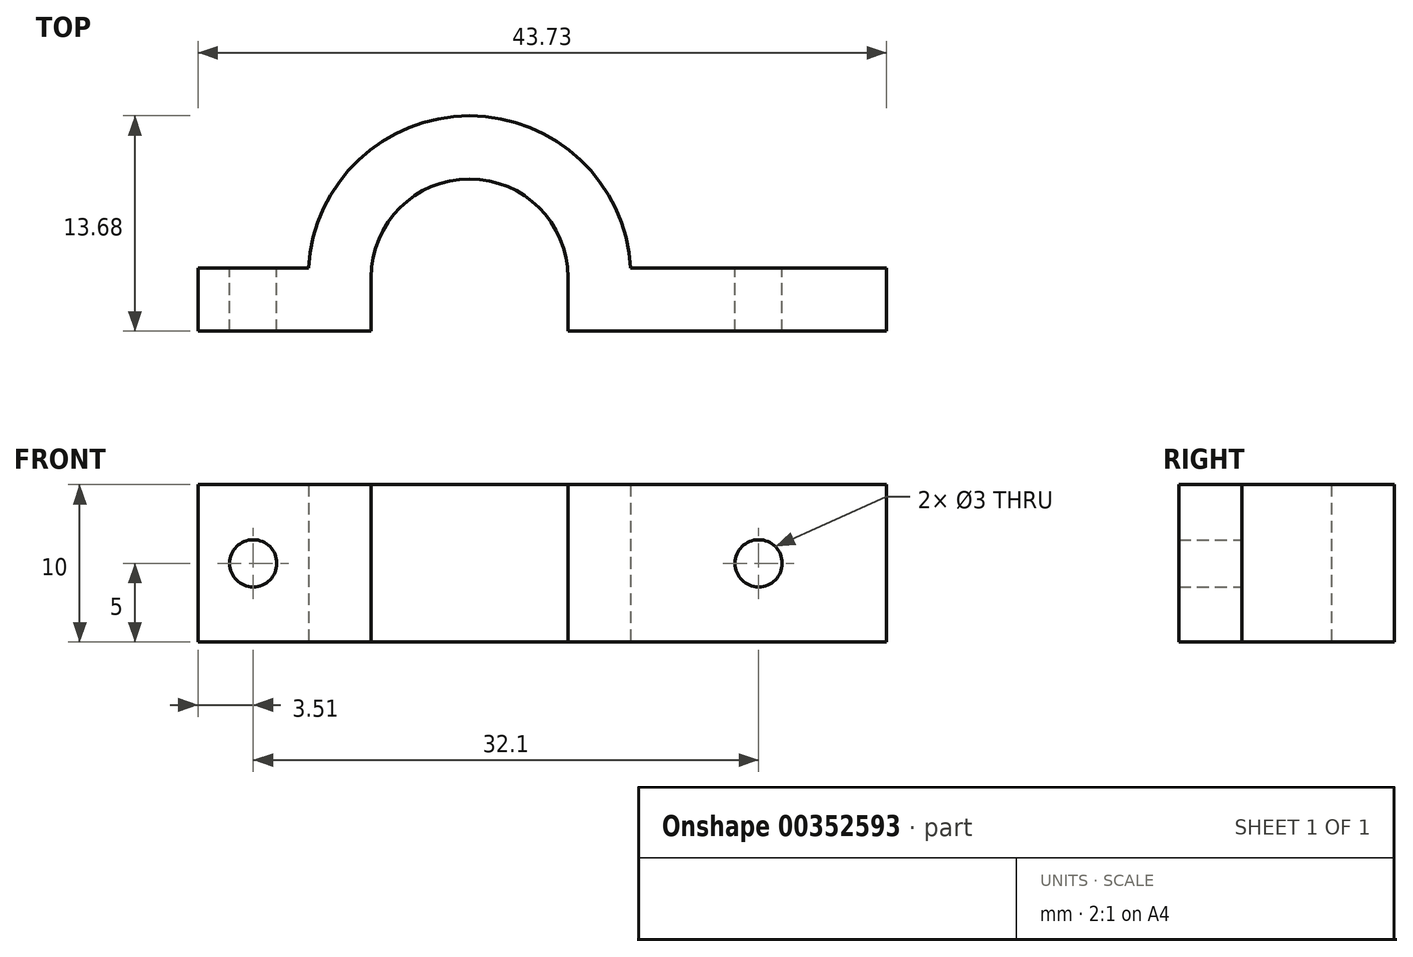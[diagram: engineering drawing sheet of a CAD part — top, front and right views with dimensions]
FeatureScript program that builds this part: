
annotation { "Feature Type Name" : "Feature", "Feature Type Description" : "" }
export const myFeature = defineFeature(function(context is Context, id is Id, definition is map)
    precondition{}
    {
        {
            var Q0;
            Q0=qCreatedBy(makeId("Top.planeOp"),FACE);
            var sketch = newSketch(context, id + "F0", { "sketchPlane" : qUnion([Q0])});
            skLineSegment(sketch, "E0", {"start": v(14.61, -13.31) * mm, "end": v(38.11, -13.31) * mm});
            skLineSegment(sketch, "E1", {"start": v(38.11, -13.31) * mm, "end": v(38.11, -9.31) * mm});
            skLineSegment(sketch, "E2", {"start": v(38.11, -9.31) * mm, "end": v(18.6, -9.31) * mm});
            skLineSegment(sketch, "E3", {"start": v(14.61, -13.31) * mm, "end": v(2.11, -13.31) * mm, "construction": true});
            skLineSegment(sketch, "E4", {"start": v(2.11, -13.31) * mm, "end": v(-8.89, -13.31) * mm});
            skLineSegment(sketch, "E5", {"start": v(-8.89, -13.31) * mm, "end": v(-8.89, -9.31) * mm});
            skLineSegment(sketch, "E6", {"start": v(-8.89, -9.31) * mm, "end": v(-1.87, -9.31) * mm});
            skLineSegment(sketch, "E7", {"start": v(14.61, -13.31) * mm, "end": v(14.61, -9.9) * mm});
            skLineSegment(sketch, "E8", {"start": v(2.11, -13.31) * mm, "end": v(2.11, -9.9) * mm});
            skArc(sketch, "E9", {"start": v(14.61, -9.9) * mm, "mid": v(8.36, -3.64) * mm, "end": v(2.11, -9.9) * mm});
            skArc(sketch, "E10", {"start": v(18.6, -9.31) * mm, "mid": v(8.36, 0.37) * mm, "end": v(-1.87, -9.31) * mm});
            skSolve(sketch);
        }
        {
            var Q0;
            Q0=qSketchRegion(id+"F0",true);
            extrude(context, id + "F1", {"entities" : qUnion([Q0]), "depth" : 10 * mm});
        }
        {
            var Q0;
            Q0=makeQuery(id+"F1.opExtrude","SWEPT_FACE",FACE,{"disambiguationData":[OSD([sQuery(id+"F0.wireOp",EDGE,"E4")])]});
            var sketch = newSketch(context, id + "F2", { "sketchPlane" : qUnion([Q0])});
            skCircle(sketch, "E11.cCircle", {"center": v(-3.89, 5) * mm, "radius": 1.5 * mm, "construction": true});
            skLineSegment(sketch, "E11.0", {"start": v(-3.02, 6.5) * mm, "end": v(-2.16, 5) * mm});
            skLineSegment(sketch, "E11.1", {"start": v(-2.16, 5) * mm, "end": v(-3.02, 3.5) * mm});
            skLineSegment(sketch, "E11.2", {"start": v(-3.02, 3.5) * mm, "end": v(-4.75, 3.5) * mm});
            skLineSegment(sketch, "E11.3", {"start": v(-4.75, 3.5) * mm, "end": v(-5.62, 5) * mm});
            skLineSegment(sketch, "E11.4", {"start": v(-5.62, 5) * mm, "end": v(-4.75, 6.5) * mm});
            skLineSegment(sketch, "E11.5", {"start": v(-4.75, 6.5) * mm, "end": v(-3.02, 6.5) * mm});
            skPoint(sketch, "E11.0.midPoint", {"position": v(-2.59, 5.75) * mm});
            skCircle(sketch, "E12.cCircle", {"center": v(29.11, 5) * mm, "radius": 1.5 * mm, "construction": true});
            skLineSegment(sketch, "E12.0", {"start": v(28.25, 6.5) * mm, "end": v(29.98, 6.5) * mm});
            skLineSegment(sketch, "E12.1", {"start": v(29.98, 6.5) * mm, "end": v(30.84, 5) * mm});
            skLineSegment(sketch, "E12.2", {"start": v(30.84, 5) * mm, "end": v(29.98, 3.5) * mm});
            skLineSegment(sketch, "E12.3", {"start": v(29.98, 3.5) * mm, "end": v(28.25, 3.5) * mm});
            skLineSegment(sketch, "E12.4", {"start": v(28.25, 3.5) * mm, "end": v(27.38, 5) * mm});
            skLineSegment(sketch, "E12.5", {"start": v(27.38, 5) * mm, "end": v(28.25, 6.5) * mm});
            skPoint(sketch, "E12.0.midPoint", {"position": v(29.11, 6.5) * mm});
            skLineSegment(sketch, "E13", {"start": v(-5.62, 5) * mm, "end": v(30.84, 5) * mm, "construction": true});
            skSolve(sketch);
        }
        {
            var Q0;
            Q0=qSketchRegion(id+"F2",true);
            extrude(context, id + "F3", {"entities" : qUnion([Q0]), "operationType" : NewBodyOperationType.REMOVE, "endBound" : BoundingType.THROUGH_ALL, "oppositeDirection" : true, "depth" : 25 * mm});
        }
        {
            var Q0;
            Q0=makeQuery(id+"F1.opExtrude","SWEPT_FACE",FACE,{"disambiguationData":[OSD([sQuery(id+"F0.wireOp",EDGE,"E1")])]});
            extrude(context, id + "F4", {"entities" : qUnion([Q0]), "operationType" : NewBodyOperationType.REMOVE, "oppositeDirection" : true, "depth" : 3.27 * mm});
        }
        {
            var Q0;
            Q0=makeQuery(id+"F1.opExtrude","SWEPT_FACE",FACE,{"disambiguationData":[OSD([sQuery(id+"F0.wireOp",EDGE,"E6")])]});
            var sketch = newSketch(context, id + "F5", { "sketchPlane" : qUnion([Q0])});
            skLineSegment(sketch, "E14", {"start": v(5.62, 5) * mm, "end": v(4.75, 3.5) * mm});
            skLineSegment(sketch, "E15", {"start": v(4.75, 3.5) * mm, "end": v(3.02, 3.5) * mm});
            skLineSegment(sketch, "E16", {"start": v(3.02, 3.5) * mm, "end": v(2.16, 5) * mm});
            skLineSegment(sketch, "E17", {"start": v(2.16, 5) * mm, "end": v(3.02, 6.5) * mm});
            skLineSegment(sketch, "E18", {"start": v(3.02, 6.5) * mm, "end": v(4.75, 6.5) * mm});
            skLineSegment(sketch, "E19", {"start": v(4.75, 6.5) * mm, "end": v(5.62, 5) * mm});
            skSolve(sketch);
        }
        {
            var Q0;
            Q0 = qSketchRegion(id + "F5", true);
            var Q1;
            Q1 = qSketchRegion(id + "F7", true);
            var Q2;
            Q2=makeQuery(id+"F1.opExtrude","SWEPT_FACE",FACE,{"disambiguationData":[OSD([sQuery(id+"F0.wireOp",EDGE,"E4")])]});
            extrude(context, id + "F6", {"entities" : qUnion([Q0, Q1]), "operationType" : NewBodyOperationType.ADD, "endBound" : BoundingType.UP_TO_SURFACE, "oppositeDirection" : true, "depth" : 25 * mm, "endBoundEntityFace" : qUnion([Q2]), "offsetDistance" : 25 * mm});
        }
        {
            var Q0;
            Q0=makeQuery(id+"F1.opExtrude","SWEPT_FACE",FACE,{"disambiguationData":[OSD([sQuery(id+"F0.wireOp",EDGE,"E2")])]});
            var sketch = newSketch(context, id + "F7", { "sketchPlane" : qUnion([Q0])});
            skLineSegment(sketch, "E20", {"start": v(-27.38, 5) * mm, "end": v(-28.25, 3.5) * mm});
            skLineSegment(sketch, "E21", {"start": v(-28.25, 3.5) * mm, "end": v(-29.98, 3.5) * mm});
            skLineSegment(sketch, "E22", {"start": v(-29.98, 3.5) * mm, "end": v(-30.84, 5) * mm});
            skLineSegment(sketch, "E23", {"start": v(-30.84, 5) * mm, "end": v(-29.98, 6.5) * mm});
            skLineSegment(sketch, "E24", {"start": v(-29.98, 6.5) * mm, "end": v(-28.25, 6.5) * mm});
            skLineSegment(sketch, "E25", {"start": v(-28.25, 6.5) * mm, "end": v(-27.38, 5) * mm});
            skSolve(sketch);
        }
        {
            var Q0;
            Q0 = qSketchRegion(id + "F7", true);
            var Q1;
            Q1=makeQuery(id+"F1.opExtrude","SWEPT_FACE",FACE,{"disambiguationData":[OSD([sQuery(id+"F0.wireOp",EDGE,"E0")])]});
            extrude(context, id + "F8", {"entities" : qUnion([Q0]), "operationType" : NewBodyOperationType.ADD, "endBound" : BoundingType.UP_TO_SURFACE, "oppositeDirection" : true, "depth" : 25 * mm, "endBoundEntityFace" : qUnion([Q1]), "offsetDistance" : 25 * mm});
        }
        {
            var Q0;
            Q0=makeQuery(id+"F6.boolean.opBoolean","MERGE",FACE,{"derivedFrom":[makeQuery(id+"F1.opExtrude","SWEPT_FACE",FACE,{"disambiguationData":[OSD([sQuery(id+"F0.wireOp",EDGE,"E6")])]}),makeQuery(id+"F6.opExtrude","CAP_FACE",FACE,{"disambiguationData":[OSD([sQuery(id+"F5.wireOp",EDGE,"E14"),sQuery(id+"F5.wireOp",EDGE,"E15"),sQuery(id+"F5.wireOp",EDGE,"E16"),sQuery(id+"F5.wireOp",EDGE,"E17"),sQuery(id+"F5.wireOp",EDGE,"E18"),sQuery(id+"F5.wireOp",EDGE,"E19")])],"isStart":true})]});
            var sketch = newSketch(context, id + "F9", { "sketchPlane" : qUnion([Q0])});
            skCircle(sketch, "E26", {"center": v(5.38, 5) * mm, "radius": 1.5 * mm});
            skCircle(sketch, "E27", {"center": v(-26.72, 5) * mm, "radius": 1.5 * mm});
            skSolve(sketch);
        }
        {
            var Q0;
            Q0 = qSketchRegion(id + "F9", true);
            extrude(context, id + "F10", {"entities" : qUnion([Q0]), "operationType" : NewBodyOperationType.REMOVE, "endBound" : BoundingType.THROUGH_ALL, "oppositeDirection" : true, "depth" : 25 * mm, "offsetDistance" : 25 * mm});
        }
    });
